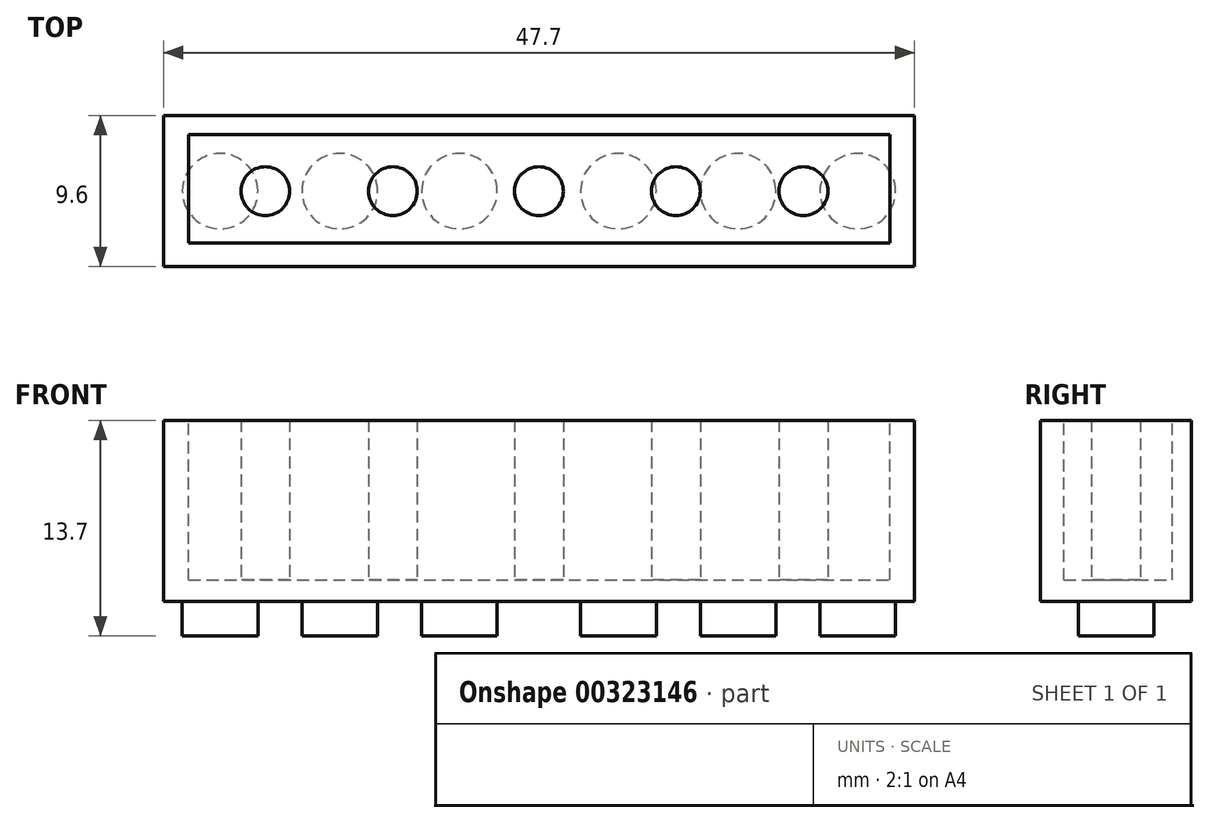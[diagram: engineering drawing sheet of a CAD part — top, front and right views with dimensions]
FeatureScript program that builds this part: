
annotation { "Feature Type Name" : "Feature", "Feature Type Description" : "" }
export const myFeature = defineFeature(function(context is Context, id is Id, definition is map)
    precondition{}
    {
        {
            var Q0;
            Q0=qCreatedBy(makeId("Top.planeOp"),FACE);
            var sketch = newSketch(context, id + "F0", { "sketchPlane" : qUnion([Q0])});
            skLineSegment(sketch, "E0.bottom", {"start": v(23.85, -4.8) * mm, "end": v(-23.85, -4.8) * mm});
            skLineSegment(sketch, "E0.top", {"start": v(23.85, 4.8) * mm, "end": v(-23.85, 4.8) * mm});
            skLineSegment(sketch, "E0.left", {"start": v(23.85, -4.8) * mm, "end": v(23.85, 4.8) * mm});
            skLineSegment(sketch, "E0.right", {"start": v(-23.85, -4.8) * mm, "end": v(-23.85, 4.8) * mm});
            skPoint(sketch, "E0.middle", {"position": v(0, 0) * mm});
            skCircle(sketch, "E1", {"center": v(-20.25, 0) * mm, "radius": 2.4 * mm});
            skCircle(sketch, "E2", {"center": v(-12.65, 0) * mm, "radius": 2.4 * mm});
            skCircle(sketch, "E3", {"center": v(-5.05, 0) * mm, "radius": 2.4 * mm});
            skCircle(sketch, "E4", {"center": v(20.25, 0) * mm, "radius": 2.4 * mm});
            skCircle(sketch, "E5", {"center": v(12.65, 0) * mm, "radius": 2.4 * mm});
            skCircle(sketch, "E6", {"center": v(5.05, 0) * mm, "radius": 2.4 * mm});
            skSolve(sketch);
        }
        {
            var Q0;
            Q0=makeQuery(id+"F0.imprint","IMPRINT",FACE,{"disambiguationData":[TD([[makeQuery(id+"F0.imprint","IMPRINT",EDGE,{"derivedFrom":sQuery(id+"F0.wireOp",EDGE,"E0.bottom")}),-1.0]])]});
            var Q1;
            Q1=makeQuery(id+"F0.imprint","IMPRINT",FACE,{"disambiguationData":[TD([[makeQuery(id+"F0.imprint","IMPRINT",EDGE,{"derivedFrom":sQuery(id+"F0.wireOp",EDGE,"E1")}),1.0]])]});
            var Q2;
            Q2=makeQuery(id+"F0.imprint","IMPRINT",FACE,{"disambiguationData":[TD([[makeQuery(id+"F0.imprint","IMPRINT",EDGE,{"derivedFrom":sQuery(id+"F0.wireOp",EDGE,"E2")}),1.0]])]});
            var Q3;
            Q3=makeQuery(id+"F0.imprint","IMPRINT",FACE,{"disambiguationData":[TD([[makeQuery(id+"F0.imprint","IMPRINT",EDGE,{"derivedFrom":sQuery(id+"F0.wireOp",EDGE,"E3")}),1.0]])]});
            var Q4;
            Q4=makeQuery(id+"F0.imprint","IMPRINT",FACE,{"disambiguationData":[TD([[makeQuery(id+"F0.imprint","IMPRINT",EDGE,{"derivedFrom":sQuery(id+"F0.wireOp",EDGE,"E6")}),1.0]])]});
            var Q5;
            Q5=makeQuery(id+"F0.imprint","IMPRINT",FACE,{"disambiguationData":[TD([[makeQuery(id+"F0.imprint","IMPRINT",EDGE,{"derivedFrom":sQuery(id+"F0.wireOp",EDGE,"E5")}),1.0]])]});
            var Q6;
            Q6=makeQuery(id+"F0.imprint","IMPRINT",FACE,{"disambiguationData":[TD([[makeQuery(id+"F0.imprint","IMPRINT",EDGE,{"derivedFrom":sQuery(id+"F0.wireOp",EDGE,"E4")}),1.0]])]});
            extrude(context, id + "F1", {"entities" : qUnion([Q0, Q1, Q2, Q3, Q4, Q5, Q6]), "depth" : 9.5 * mm});
        }
        {
            var Q0;
            Q0=makeQuery(id+"F0.imprint","IMPRINT",FACE,{"disambiguationData":[TD([[makeQuery(id+"F0.imprint","IMPRINT",EDGE,{"derivedFrom":sQuery(id+"F0.wireOp",EDGE,"E1")}),1.0]])]});
            var Q1;
            Q1=makeQuery(id+"F0.imprint","IMPRINT",FACE,{"disambiguationData":[TD([[makeQuery(id+"F0.imprint","IMPRINT",EDGE,{"derivedFrom":sQuery(id+"F0.wireOp",EDGE,"E2")}),1.0]])]});
            var Q2;
            Q2=makeQuery(id+"F0.imprint","IMPRINT",FACE,{"disambiguationData":[TD([[makeQuery(id+"F0.imprint","IMPRINT",EDGE,{"derivedFrom":sQuery(id+"F0.wireOp",EDGE,"E3")}),1.0]])]});
            var Q3;
            Q3=makeQuery(id+"F0.imprint","IMPRINT",FACE,{"disambiguationData":[TD([[makeQuery(id+"F0.imprint","IMPRINT",EDGE,{"derivedFrom":sQuery(id+"F0.wireOp",EDGE,"E6")}),1.0]])]});
            var Q4;
            Q4=makeQuery(id+"F0.imprint","IMPRINT",FACE,{"disambiguationData":[TD([[makeQuery(id+"F0.imprint","IMPRINT",EDGE,{"derivedFrom":sQuery(id+"F0.wireOp",EDGE,"E5")}),1.0]])]});
            var Q5;
            Q5=makeQuery(id+"F0.imprint","IMPRINT",FACE,{"disambiguationData":[TD([[makeQuery(id+"F0.imprint","IMPRINT",EDGE,{"derivedFrom":sQuery(id+"F0.wireOp",EDGE,"E4")}),1.0]])]});
            extrude(context, id + "F2", {"entities" : qUnion([Q0, Q1, Q2, Q3, Q4, Q5]), "operationType" : NewBodyOperationType.ADD, "oppositeDirection" : true, "depth" : 2.2 * mm});
        }
        {
            var Q0;
            Q0=qCreatedBy(makeId("Top.planeOp"),FACE);
            var sketch = newSketch(context, id + "F3", { "sketchPlane" : qUnion([Q0])});
            skCircle(sketch, "E7", {"center": v(-12.5, 0) * mm, "radius": 1.55 * mm});
            skCircle(sketch, "E8", {"center": v(-19.1, 0) * mm, "radius": 1.55 * mm});
            skCircle(sketch, "E9", {"center": v(0, 0) * mm, "radius": 2.07 * mm});
            skCircle(sketch, "E10", {"center": v(12.52, 0) * mm, "radius": 1.55 * mm});
            skCircle(sketch, "E11", {"center": v(19.12, 0) * mm, "radius": 1.55 * mm});
            skLineSegment(sketch, "E12.bottom", {"start": v(22.13, 3.3) * mm, "end": v(-22.13, 3.3) * mm});
            skLineSegment(sketch, "E12.top", {"start": v(22.13, -3.3) * mm, "end": v(-22.13, -3.3) * mm});
            skLineSegment(sketch, "E12.left", {"start": v(22.13, 3.3) * mm, "end": v(22.13, -3.3) * mm});
            skLineSegment(sketch, "E12.right", {"start": v(-22.13, 3.3) * mm, "end": v(-22.13, -3.3) * mm});
            skSolve(sketch);
        }
        {
            var Q0;
            Q0 = qSketchRegion(id + "F3", true);
            var Q1;
            Q1=makeQuery(id+"F1.opExtrude","CAP_FACE",FACE,{"disambiguationData":[OSD([sQuery(id+"F0.wireOp",EDGE,"E0.bottom"),sQuery(id+"F0.wireOp",EDGE,"E0.top"),sQuery(id+"F0.wireOp",EDGE,"E0.left"),sQuery(id+"F0.wireOp",EDGE,"E0.right")])],"isStart":false});
            extrude(context, id + "F4", {"entities" : qUnion([Q0, Q1]), "operationType" : NewBodyOperationType.ADD, "depth" : 2 * mm});
        }
        {
            var Q0;
            Q0=makeQuery(id+"F4.opExtrude","CAP_FACE",FACE,{"disambiguationData":[OSD([sQuery(id+"F0.wireOp",EDGE,"E0.bottom"),sQuery(id+"F0.wireOp",EDGE,"E0.top"),sQuery(id+"F0.wireOp",EDGE,"E0.left"),sQuery(id+"F0.wireOp",EDGE,"E0.right")])],"isStart":false});
            var sketch = newSketch(context, id + "F5", { "sketchPlane" : qUnion([Q0])});
            skLineSegment(sketch, "E13.bottom", {"start": v(-22.26, -3.3) * mm, "end": v(22.28, -3.3) * mm});
            skLineSegment(sketch, "E13.top", {"start": v(-22.26, 3.6) * mm, "end": v(22.28, 3.6) * mm});
            skLineSegment(sketch, "E13.left", {"start": v(-22.26, -3.3) * mm, "end": v(-22.26, 3.6) * mm});
            skLineSegment(sketch, "E13.right", {"start": v(22.28, -3.3) * mm, "end": v(22.28, 3.6) * mm});
            skSolve(sketch);
        }
        {
            var Q0;
            Q0=makeQuery(id+"F5.imprint","IMPRINT",FACE,{"disambiguationData":[TD([[makeQuery(id+"F5.imprint","IMPRINT",EDGE,{"derivedFrom":sQuery(id+"F5.wireOp",EDGE,"E13.bottom")}),1.0]])]});
            extrude(context, id + "F6", {"entities" : qUnion([Q0]), "operationType" : NewBodyOperationType.REMOVE, "oppositeDirection" : true, "depth" : 10.15 * mm});
        }
        {
            var Q0;
            Q0=makeQuery(id+"F6.boolean.opBoolean","COPY",FACE,{"derivedFrom":makeQuery(id+"F6.opExtrude","CAP_FACE",FACE,{"disambiguationData":[OSD([sQuery(id+"F5.wireOp",EDGE,"E13.bottom"),sQuery(id+"F5.wireOp",EDGE,"E13.top"),sQuery(id+"F5.wireOp",EDGE,"E13.left"),sQuery(id+"F5.wireOp",EDGE,"E13.right")])],"isStart":false})});
            var sketch = newSketch(context, id + "F7", { "sketchPlane" : qUnion([Q0])});
            skCircle(sketch, "E14", {"center": v(-9.28, 0) * mm, "radius": 1.55 * mm});
            skCircle(sketch, "E15", {"center": v(-17.38, 0) * mm, "radius": 1.55 * mm});
            skCircle(sketch, "E16", {"center": v(8.7, 0) * mm, "radius": 1.55 * mm});
            skCircle(sketch, "E17", {"center": v(16.8, 0) * mm, "radius": 1.55 * mm});
            skCircle(sketch, "E18", {"center": v(0, 0) * mm, "radius": 1.55 * mm});
            skSolve(sketch);
        }
        {
            var Q0;
            Q0=makeQuery(id+"F7.imprint","IMPRINT",FACE,{"disambiguationData":[TD([[makeQuery(id+"F7.imprint","IMPRINT",EDGE,{"derivedFrom":sQuery(id+"F7.wireOp",EDGE,"E15")}),1.0]])]});
            var Q1;
            Q1=makeQuery(id+"F7.imprint","IMPRINT",FACE,{"disambiguationData":[TD([[makeQuery(id+"F7.imprint","IMPRINT",EDGE,{"derivedFrom":sQuery(id+"F7.wireOp",EDGE,"E14")}),1.0]])]});
            var Q2;
            Q2=makeQuery(id+"F7.imprint","IMPRINT",FACE,{"disambiguationData":[TD([[makeQuery(id+"F7.imprint","IMPRINT",EDGE,{"derivedFrom":sQuery(id+"F7.wireOp",EDGE,"E18")}),1.0]])]});
            var Q3;
            Q3=makeQuery(id+"F7.imprint","IMPRINT",FACE,{"disambiguationData":[TD([[makeQuery(id+"F7.imprint","IMPRINT",EDGE,{"derivedFrom":sQuery(id+"F7.wireOp",EDGE,"E16")}),1.0]])]});
            var Q4;
            Q4=makeQuery(id+"F7.imprint","IMPRINT",FACE,{"disambiguationData":[TD([[makeQuery(id+"F7.imprint","IMPRINT",EDGE,{"derivedFrom":sQuery(id+"F7.wireOp",EDGE,"E17")}),1.0]])]});
            extrude(context, id + "F8", {"entities" : qUnion([Q0, Q1, Q2, Q3, Q4]), "operationType" : NewBodyOperationType.ADD, "depth" : 10.15 * mm});
        }
    });
